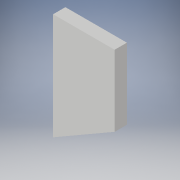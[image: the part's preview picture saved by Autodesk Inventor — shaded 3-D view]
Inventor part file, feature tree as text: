
AUTODESK INVENTOR PART (.ipt)
format: ipt  version: 2017 (Build 210142000, 142)  size: 93,184 bytes
history: native  units: in
note: dims shown in document units (in); Inventor stores cm internally (conversion verified against a paired STEP export)
features: extrude x1, sketch x1
ambient origin geometry x8: Origin, YZ Plane, XZ Plane, XY Plane, X Axis, Y Axis, Z Axis, Center Point
bodies: Solid1 (feature_tree)
feature tree (2):
  extrude  "door"  [1 undecoded]
  sketch  "Sketch1"  dims[d143=10.0in d144=0.0in]
note: 1 required parameter value undecoded (feature->parameter linkage not recoverable at this tier; creation-order binding heuristic only, values carry confidence <= 0.55)
